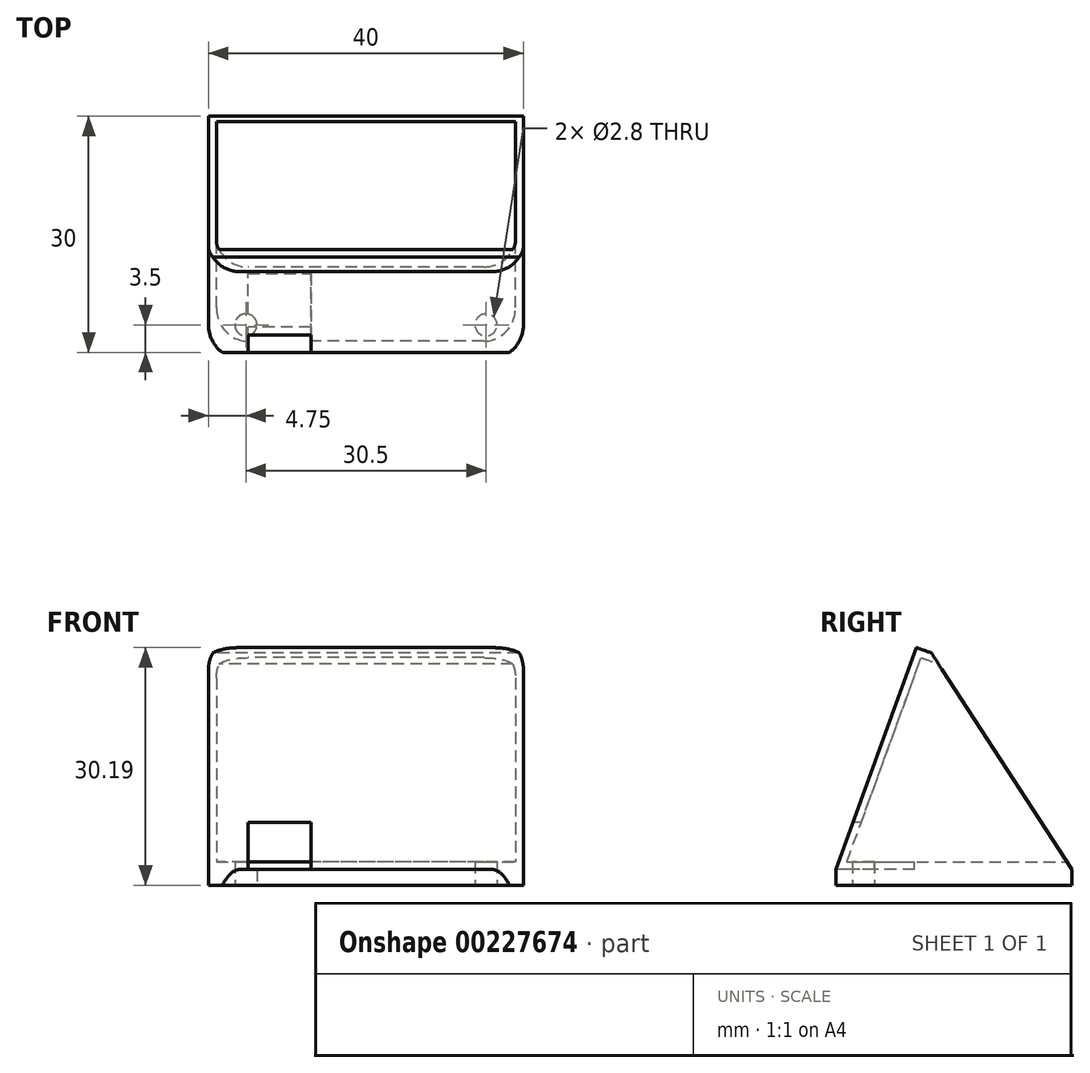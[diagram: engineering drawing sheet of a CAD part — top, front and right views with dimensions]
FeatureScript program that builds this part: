
annotation { "Feature Type Name" : "Feature", "Feature Type Description" : "" }
export const myFeature = defineFeature(function(context is Context, id is Id, definition is map)
    precondition{}
    {
        {
            var Q0;
            Q0=qCreatedBy(makeId("Right.planeOp"),FACE);
            var sketch = newSketch(context, id + "F0", { "sketchPlane" : qUnion([Q0])});
            skLineSegment(sketch, "E0", {"start": v(0, 0) * mm, "end": v(10.26, 28.2) * mm});
            skLineSegment(sketch, "E1", {"start": v(44.1, 0) * mm, "end": v(0, 0) * mm, "construction": true});
            skLineSegment(sketch, "E2", {"start": v(10.26, 28.2) * mm, "end": v(12.14, 27.5) * mm});
            skLineSegment(sketch, "E3.bottom", {"start": v(0, 0) * mm, "end": v(30, 0) * mm});
            skLineSegment(sketch, "E3.top", {"start": v(0, -2) * mm, "end": v(30, -2) * mm});
            skLineSegment(sketch, "E3.left", {"start": v(0, 0) * mm, "end": v(0, -2) * mm});
            skLineSegment(sketch, "E3.right", {"start": v(30, 0) * mm, "end": v(30, -2) * mm});
            skLineSegment(sketch, "E4", {"start": v(12.14, 27.5) * mm, "end": v(30, 0) * mm});
            skSolve(sketch);
        }
        {
            var Q0;
            Q0=makeQuery(id+"F0.imprint","IMPRINT",FACE,{"disambiguationData":[TD([[makeQuery(id+"F0.imprint","IMPRINT",EDGE,{"derivedFrom":sQuery(id+"F0.wireOp",EDGE,"E0")}),-1.0]])]});
            extrude(context, id + "F1", {"entities" : qUnion([Q0]), "depth" : 40 * mm});
        }
        {
            var Q0;
            Q0=makeQuery(id+"F1.opExtrude","SWEPT_FACE",FACE,{"disambiguationData":[OSD([sQuery(id+"F0.wireOp",EDGE,"E4")])]});
            shell(context, id + "F2", {"entities" : qUnion([Q0]), "thickness" : 1 * mm});
        }
        {
            var Q0;
            Q0=makeQuery(id+"F0.imprint","IMPRINT",FACE,{"disambiguationData":[TD([[makeQuery(id+"F0.imprint","IMPRINT",EDGE,{"derivedFrom":sQuery(id+"F0.wireOp",EDGE,"E3.bottom")}),-1.0]])]});
            extrude(context, id + "F3", {"entities" : qUnion([Q0]), "operationType" : NewBodyOperationType.ADD, "depth" : 40 * mm});
        }
        {
            var Q0;
            Q0=qCreatedBy(makeId("Front.planeOp"),FACE);
            var sketch = newSketch(context, id + "F4", { "sketchPlane" : qUnion([Q0])});
            skLineSegment(sketch, "E5.0.0", {"start": v(0, 28.2) * mm, "end": v(0, 0) * mm});
            skLineSegment(sketch, "E5.0.1", {"start": v(0, 0) * mm, "end": v(40, 0) * mm});
            skLineSegment(sketch, "E5.0.2", {"start": v(40, 0) * mm, "end": v(40, 28.2) * mm});
            skLineSegment(sketch, "E5.0.3", {"start": v(40, 28.2) * mm, "end": v(0, 28.2) * mm});
            skLineSegment(sketch, "E5.1.3", {"start": v(40, 0) * mm, "end": v(0, 0) * mm});
            skLineSegment(sketch, "E6", {"start": v(0, 14.1) * mm, "end": v(40, 14.1) * mm, "construction": true});
            skLineSegment(sketch, "E7", {"start": v(20, 28.2) * mm, "end": v(20, 0) * mm, "construction": true});
            skLineSegment(sketch, "E8", {"start": v(20, 0) * mm, "end": v(9, 0) * mm, "construction": true});
            skLineSegment(sketch, "E9", {"start": v(9, 0) * mm, "end": v(9, 2) * mm, "construction": true});
            skLineSegment(sketch, "E10.bottom", {"start": v(13, -2) * mm, "end": v(5, -2) * mm});
            skLineSegment(sketch, "E10.top", {"start": v(13, 6) * mm, "end": v(5, 6) * mm});
            skLineSegment(sketch, "E10.left", {"start": v(13, -2) * mm, "end": v(13, 6) * mm});
            skLineSegment(sketch, "E10.right", {"start": v(5, -2) * mm, "end": v(5, 6) * mm});
            skPoint(sketch, "E10.middle", {"position": v(9, 2) * mm});
            skSolve(sketch);
        }
        {
            var Q0;
            {var subQ5=sQuery(id+"F4.wireOp",EDGE,"E10.top");Q0=makeQuery(id+"F4.imprint","IMPRINT",FACE,{"disambiguationData":[TD([[makeQuery(id+"F4.imprint","IMPRINT",EDGE,{"derivedFrom":subQ5}),1.0]])]});}
            extrude(context, id + "F5", {"entities" : qUnion([Q0]), "operationType" : NewBodyOperationType.REMOVE, "oppositeDirection" : true, "depth" : 10 * mm});
        }
        {
            var Q0;
            Q0=makeQuery(id+"F3.opExtrude","SWEPT_FACE",FACE,{"disambiguationData":[OSD([sQuery(id+"F0.wireOp",EDGE,"E3.top")])]});
            var sketch = newSketch(context, id + "F6", { "sketchPlane" : qUnion([Q0])});
            skPoint(sketch, "E11.startSnap0", {"position": v(20, 0) * mm});
            skLineSegment(sketch, "E12", {"start": v(4.75, -3.5) * mm, "end": v(20, -3.5) * mm, "construction": true});
            skLineSegment(sketch, "E13", {"start": v(35.25, -3.5) * mm, "end": v(20, -3.5) * mm, "construction": true});
            skLineSegment(sketch, "E14", {"start": v(20, -3.5) * mm, "end": v(20, 0) * mm, "construction": true});
            skCircle(sketch, "E15", {"center": v(4.75, -3.5) * mm, "radius": 1.4 * mm});
            skCircle(sketch, "E16", {"center": v(35.25, -3.5) * mm, "radius": 1.4 * mm});
            skSolve(sketch);
        }
        {
            var Q0;
            Q0=makeQuery(id+"F6.imprint","IMPRINT",FACE,{"disambiguationData":[TD([[makeQuery(id+"F6.imprint","IMPRINT",EDGE,{"derivedFrom":sQuery(id+"F6.wireOp",EDGE,"E15")}),1.0]])]});
            var Q1;
            Q1=makeQuery(id+"F6.imprint","IMPRINT",FACE,{"disambiguationData":[TD([[makeQuery(id+"F6.imprint","IMPRINT",EDGE,{"derivedFrom":sQuery(id+"F6.wireOp",EDGE,"E16")}),1.0]])]});
            extrude(context, id + "F7", {"entities" : qUnion([Q0, Q1]), "operationType" : NewBodyOperationType.REMOVE, "oppositeDirection" : true, "depth" : 3 * mm});
        }
        {
            var Q0;
            {var subQ0=sQuery(id+"F0.wireOp",EDGE,"E0");Q0=makeQuery(id+"F2.opShell","OFFSET_EDGE",EDGE,{"disambiguationData":[OSD([subQ0]),TDD([makeQuery(id+"F1.opExtrude","CAP_EDGE",EDGE,{"disambiguationData":[OSD([subQ0])],"isStart":true})])]});}
            var Q1;
            {var subQ0=sQuery(id+"F0.wireOp",EDGE,"E0");Q1=makeQuery(id+"F2.opShell","OFFSET_EDGE",EDGE,{"disambiguationData":[OSD([subQ0]),TDD([makeQuery(id+"F1.opExtrude","CAP_EDGE",EDGE,{"disambiguationData":[OSD([subQ0])],"isStart":false})])]});}
            var Q2;
            {var subQ0=sQuery(id+"F0.wireOp",EDGE,"E3.top");Q2=makeQuery(id+"F2.opShell","OFFSET_EDGE",EDGE,{"disambiguationData":[OSD([subQ0]),TDD([makeQuery(id+"F1.opExtrude","CAP_EDGE",EDGE,{"disambiguationData":[OSD([subQ0])],"isStart":false})])]});}
            var Q3;
            {var subQ0=sQuery(id+"F0.wireOp",EDGE,"E3.top");Q3=makeQuery(id+"F2.opShell","OFFSET_EDGE",EDGE,{"disambiguationData":[OSD([subQ0]),TDD([makeQuery(id+"F1.opExtrude","CAP_EDGE",EDGE,{"disambiguationData":[OSD([subQ0])],"isStart":true})])]});}
            var Q4;
            Q4=makeQuery(id+"F1.opExtrude","CAP_EDGE",EDGE,{"disambiguationData":[OSD([sQuery(id+"F0.wireOp",EDGE,"E0")])],"isStart":true});
            var Q5;
            Q5=makeQuery(id+"F1.opExtrude","CAP_EDGE",EDGE,{"disambiguationData":[OSD([sQuery(id+"F0.wireOp",EDGE,"E0")])],"isStart":false});
            fillet(context, id + "F8", {"entities" : qUnion([Q0, Q1, Q2, Q3, Q4, Q5]), "radius" : 4 * mm, "tangentPropagation" : true, "allowEdgeOverflow" : false});
        }
    });
